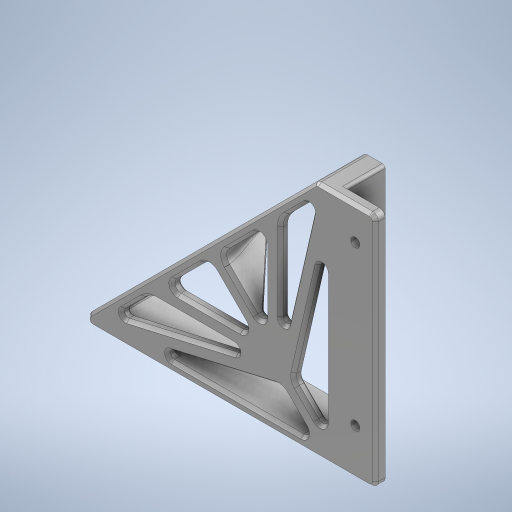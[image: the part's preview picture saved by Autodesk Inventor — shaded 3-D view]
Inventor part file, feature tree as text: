
AUTODESK INVENTOR PART (.ipt)
format: ipt  version: 2024.1 (Build 281209000, 209)  size: 970,752 bytes
history: native  units: mm
features: fillet x14, sketch x6, extrude x5, chamfer x5, hole x2, projected_geometry x1
ambient origin geometry x8: Origin, YZ Plane, XZ Plane, XY Plane, X Axis, Y Axis, Z Axis, Center Point
bodies: Body1 (feature_tree)
feature tree (33):
  extrude  "Extrusion3"  Depth=4.0mm
  fillet  "Fillet2"  Radius=165.0mm
  hole  "Hole4"  [1 undecoded]
  sketch  "Sketch7"  dims[d46=3.0mm]
  extrude  "Extrusion5"  Depth=10.0mm
  extrude  "Extrusion6"  Depth=23.285mm
  fillet  "Fillet4"  Radius=5.0mm
  fillet  "Fillet6"  Radius=20.0mm
  extrude  "Extrusion7"  Depth=10.0mm
  hole  "Hole6"  [1 undecoded]
  fillet  "Fillet9"  Radius=7.5mm
  fillet  "Fillet10"  Radius=20.0mm
  fillet  "Fillet11"  Radius=5.0mm
  fillet  "Fillet13"  [1 undecoded]
  fillet  "Fillet17"  Radius=3.0mm
  fillet  "Fillet19"  Radius=3.75mm
  fillet  "Fillet22"  Radius=5.0mm
  chamfer  "Chamfer5"  Distance=11.0mm
  chamfer  "Chamfer4"  Distance=15.0mm
  extrude  "Extrusion10"  Depth=10.0mm
  fillet  "Fillet23"  Radius=15.24mm
  fillet  "Fillet24"  Radius=10.0mm
  fillet  "Fillet25"  Radius=7.62mm
  chamfer  "Chamfer9"  Distance=54.952633mm
  fillet  "Fillet27"  Radius=49.952633mm
  chamfer  "Chamfer3"  Distance=1.5mm
  chamfer  "Chamfer10"  Distance=8.0mm
  sketch  "Sketch1"  dims[d3=30.0mm d41=4.0mm d42=165.0mm]
  sketch  "Sketch6"  dims[d43=45.0deg d44=5.0mm d45=0.0mm]
  sketch  "Sketch10"  dims[d47=4.5mm d48=6.0mm d49=9.4mm d50=2.0mm d51=90.0deg d52=39.95mm d53=0.0mm d54=10.0mm]
  sketch  "Sketch11"  dims[d55=80.0mm d56=23.285mm d57=5.0mm d58=20.0mm]
  sketch  "Sketch15"  dims[d61=7.5mm d63=7.5mm d66=3.75mm d67=7.5mm d68=20.0mm d69=0.0mm d70=5.0mm d71=0.0mm d72=0.0mm d74=3.0mm d75=3.75mm d77=5.0mm d91=11.0mm d93=15.0mm d95=62.25mm d96=15.24mm d97=10.0mm d98=0.0mm d101=6.2mm d102=6.0mm d103=9.4mm d104=2.0mm d105=90.0deg d106=8.0mm d107=0.0mm d108=7.62mm d111=54.952633mm d112=49.952633mm d115=1.5mm d116=8.0mm d117=2.0mm d124=10.0mm d131=1.0mm d132=1.4mm d133=2.0mm d134=8.726646mm d137=1.5mm d140=3.0mm d141=1.4mm d142=2.0mm d143=6.981317mm d144=20.0mm d145=2.0mm d146=8.988446mm d153=10.0mm d154=0.0mm d155=2.0mm d156=0.5mm d157=1.0mm d162=1.0mm d163=2.0mm d164=45.0deg d166=0.0mm d167=5.0mm d168=0.0mm d169=5.0mm d170=1.0mm d171=2.0mm d172=45.0deg d118=0.0mm d119=0.0mm d120=0.0mm d125=0.5mm d126=0.872665mm d127=0.5mm d128=0.872665mm d129=0.0mm d130=0.0mm]
  projected_geometry  "Project Cut Edges1"
note: 3 required parameter values undecoded (feature->parameter linkage not recoverable at this tier; creation-order binding heuristic only, values carry confidence <= 0.55)
